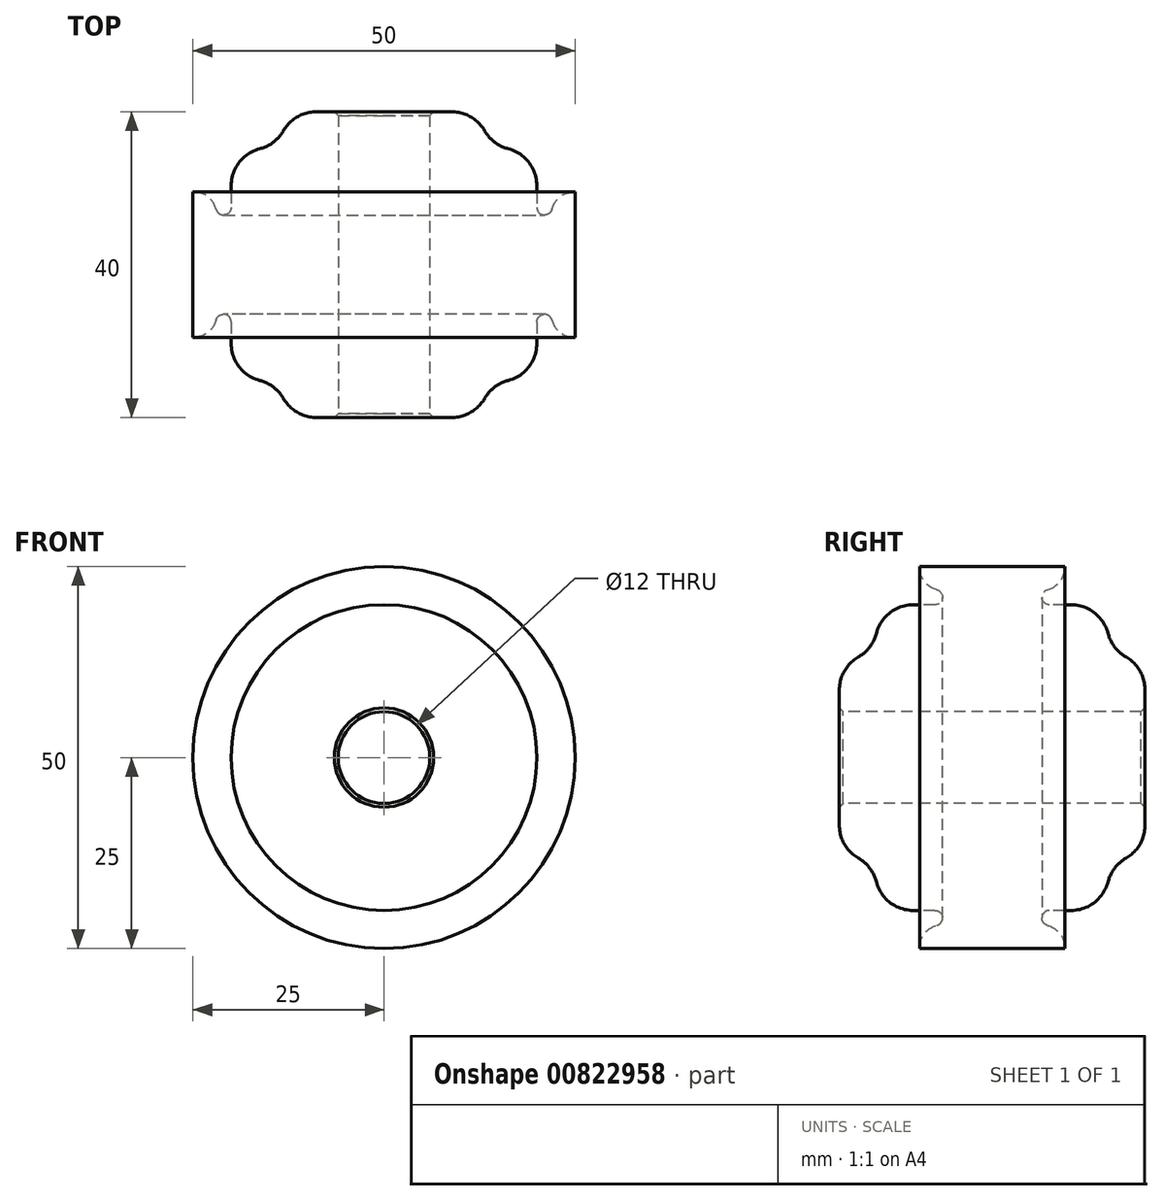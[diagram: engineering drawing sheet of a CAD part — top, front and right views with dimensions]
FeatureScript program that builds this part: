
annotation { "Feature Type Name" : "Feature", "Feature Type Description" : "" }
export const myFeature = defineFeature(function(context is Context, id is Id, definition is map)
    precondition{}
    {
        {
            var Q0;
            Q0=qCreatedBy(makeId("Top.planeOp"),FACE);
            var sketch = newSketch(context, id + "F0", { "sketchPlane" : qUnion([Q0])});
            skLineSegment(sketch, "E0", {"start": v(0, 0) * mm, "end": v(0, 35.03) * mm, "construction": true});
            skLineSegment(sketch, "E1", {"start": v(0, 0) * mm, "end": v(-25, 0) * mm, "construction": true});
            skLineSegment(sketch, "E2", {"start": v(-25, 0) * mm, "end": v(-25, 9.5) * mm});
            skLineSegment(sketch, "E3", {"start": v(-25, 0) * mm, "end": v(-25, -9.5) * mm});
            skLineSegment(sketch, "E4", {"start": v(-6, 0) * mm, "end": v(-6, 20) * mm});
            skLineSegment(sketch, "E5", {"start": v(-6, 20) * mm, "end": v(-6, -20) * mm});
            skLineSegment(sketch, "E6", {"start": v(-6, 20) * mm, "end": v(-12.5, 20) * mm});
            skLineSegment(sketch, "E7", {"start": v(-12.5, 20) * mm, "end": v(-12.5, 15) * mm});
            skLineSegment(sketch, "E8", {"start": v(-12.5, 15) * mm, "end": v(-20, 15) * mm});
            skLineSegment(sketch, "E9", {"start": v(-20, 15) * mm, "end": v(-20, 6.5) * mm});
            skLineSegment(sketch, "E10", {"start": v(-22, 9.5) * mm, "end": v(-25, 9.5) * mm});
            skLineSegment(sketch, "E11", {"start": v(-22, 9.5) * mm, "end": v(-22, 6.5) * mm});
            skLineSegment(sketch, "E12", {"start": v(-22, 6.5) * mm, "end": v(-20, 6.5) * mm});
            skLineSegment(sketch, "E13.MirrorCS", {"start": v(-6, -20) * mm, "end": v(-12.5, -20) * mm});
            skLineSegment(sketch, "E14.MirrorCS", {"start": v(-12.5, -20) * mm, "end": v(-12.5, -15) * mm});
            skLineSegment(sketch, "E15.MirrorCS", {"start": v(-12.5, -15) * mm, "end": v(-20, -15) * mm});
            skLineSegment(sketch, "E16.MirrorCS", {"start": v(-20, -15) * mm, "end": v(-20, -6.5) * mm});
            skLineSegment(sketch, "E17.MirrorCS", {"start": v(-22, -6.5) * mm, "end": v(-20, -6.5) * mm});
            skLineSegment(sketch, "E18.MirrorCS", {"start": v(-22, -9.5) * mm, "end": v(-22, -6.5) * mm});
            skLineSegment(sketch, "E19.MirrorCS", {"start": v(-22, -9.5) * mm, "end": v(-25, -9.5) * mm});
            skSolve(sketch);
        }
        {
            var Q0;
            Q0 = qSketchRegion(id + "F0", true);
            var Q1;
            Q1=sQuery(id+"F0.wireOp",EDGE,"E0");
            revolve(context, id + "F1", {"surfaceOperationType" : NewSurfaceOperationType.NEW, "entities" : qUnion([Q0]), "axis" : qUnion([Q1]), "revolveType" : RevolveType.FULL});
        }
        {
            var Q0;
            Q0=makeQuery(id+"F1.opRevolve","SWEPT_FACE",FACE,{"disambiguationData":[OSD([sQuery(id+"F0.wireOp",EDGE,"E17.MirrorCS")])]});
            var Q1;
            Q1=makeQuery(id+"F1.opRevolve","SWEPT_FACE",FACE,{"disambiguationData":[OSD([sQuery(id+"F0.wireOp",EDGE,"E12")])]});
            fillet(context, id + "F2", {"entities" : qUnion([Q0, Q1]), "radius" : 1 * mm, "tangentPropagation" : true, "allowEdgeOverflow" : false});
        }
        {
            var Q0;
            Q0=makeQuery(id+"F1.opRevolve","SWEPT_EDGE",EDGE,{"disambiguationData":[OSD([sQuery(id+"F0.wireOp",EDGE,"E18.MirrorCS"),sQuery(id+"F0.wireOp",EDGE,"E19.MirrorCS")])]});
            var Q1;
            Q1=makeQuery(id+"F1.opRevolve","SWEPT_EDGE",EDGE,{"disambiguationData":[OSD([sQuery(id+"F0.wireOp",EDGE,"E10"),sQuery(id+"F0.wireOp",EDGE,"E11")])]});
            fillet(context, id + "F3", {"entities" : qUnion([Q0, Q1]), "radius" : 3 * mm, "tangentPropagation" : true, "allowEdgeOverflow" : false});
        }
        {
            var Q0;
            Q0=makeQuery(id+"F1.opRevolve","SWEPT_EDGE",EDGE,{"disambiguationData":[OSD([sQuery(id+"F0.wireOp",EDGE,"E7"),sQuery(id+"F0.wireOp",EDGE,"E8")])]});
            var Q1;
            Q1=makeQuery(id+"F1.opRevolve","SWEPT_EDGE",EDGE,{"disambiguationData":[OSD([sQuery(id+"F0.wireOp",EDGE,"E14.MirrorCS"),sQuery(id+"F0.wireOp",EDGE,"E15.MirrorCS")])]});
            fillet(context, id + "F4", {"entities" : qUnion([Q0, Q1]), "radius" : 5 * mm, "tangentPropagation" : true, "allowEdgeOverflow" : false});
        }
        {
            var Q0;
            Q0=makeQuery(id+"F4.opFillet","BLEND_EDGE",EDGE,{"blendedFrom":[makeQuery(id+"F1.opRevolve","SWEPT_EDGE",EDGE,{"disambiguationData":[OSD([sQuery(id+"F0.wireOp",EDGE,"E7"),sQuery(id+"F0.wireOp",EDGE,"E8")])]}),makeQuery(id+"F1.opRevolve","SWEPT_FACE",FACE,{"disambiguationData":[OSD([sQuery(id+"F0.wireOp",EDGE,"E6")])]})],"blendedInto":[makeQuery(id+"F1.opRevolve","SWEPT_FACE",FACE,{"disambiguationData":[OSD([sQuery(id+"F0.wireOp",EDGE,"E6")])]})]});
            var Q1;
            Q1=makeQuery(id+"F4.opFillet","BLEND_EDGE",EDGE,{"blendedFrom":[makeQuery(id+"F1.opRevolve","SWEPT_EDGE",EDGE,{"disambiguationData":[OSD([sQuery(id+"F0.wireOp",EDGE,"E14.MirrorCS"),sQuery(id+"F0.wireOp",EDGE,"E15.MirrorCS")])]}),makeQuery(id+"F1.opRevolve","SWEPT_FACE",FACE,{"disambiguationData":[OSD([sQuery(id+"F0.wireOp",EDGE,"E13.MirrorCS")])]})],"blendedInto":[makeQuery(id+"F1.opRevolve","SWEPT_FACE",FACE,{"disambiguationData":[OSD([sQuery(id+"F0.wireOp",EDGE,"E13.MirrorCS")])]})]});
            fillet(context, id + "F5", {"entities" : qUnion([Q0, Q1]), "radius" : 5 * mm, "tangentPropagation" : true, "allowEdgeOverflow" : false});
        }
        {
            var Q0;
            Q0=makeQuery(id+"F1.opRevolve","SWEPT_EDGE",EDGE,{"disambiguationData":[OSD([sQuery(id+"F0.wireOp",EDGE,"E15.MirrorCS"),sQuery(id+"F0.wireOp",EDGE,"E16.MirrorCS")])]});
            var Q1;
            Q1=makeQuery(id+"F1.opRevolve","SWEPT_EDGE",EDGE,{"disambiguationData":[OSD([sQuery(id+"F0.wireOp",EDGE,"E8"),sQuery(id+"F0.wireOp",EDGE,"E9")])]});
            fillet(context, id + "F6", {"entities" : qUnion([Q0, Q1]), "radius" : 5 * mm, "tangentPropagation" : true, "allowEdgeOverflow" : false});
        }
        {
            var Q0;
            Q0=makeQuery(id+"F1.opRevolve","SWEPT_FACE",FACE,{"disambiguationData":[OSD([sQuery(id+"F0.wireOp",EDGE,"E5")])]});
            chamfer(context, id + "F7", {"entities" : qUnion([Q0]), "width" : 0.5 * mm, "tangentPropagation" : true});
        }
    });
